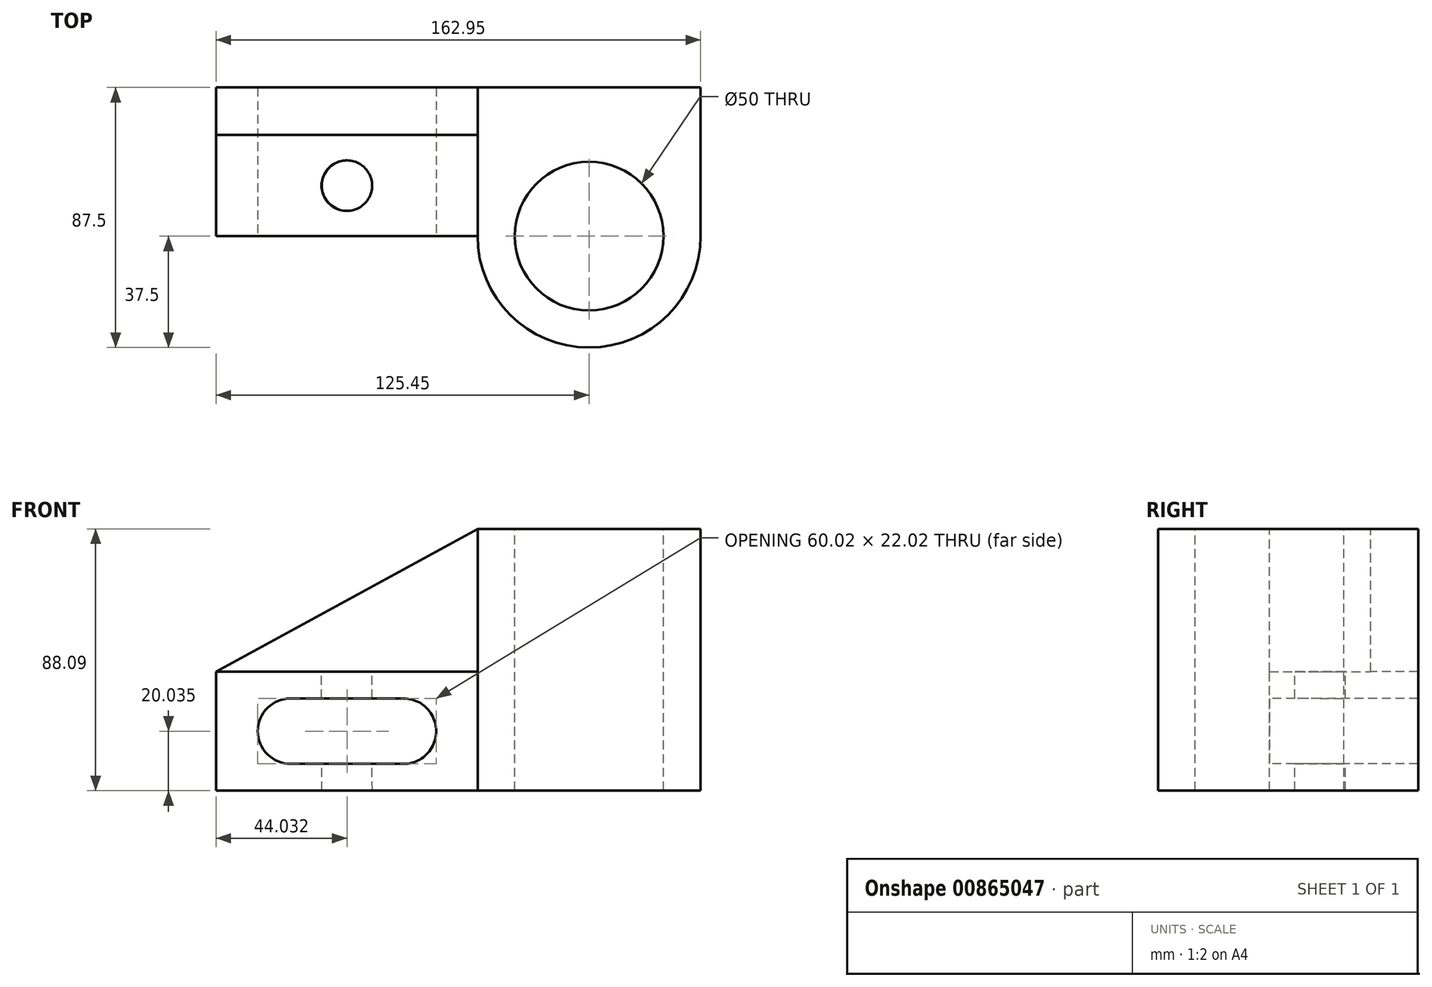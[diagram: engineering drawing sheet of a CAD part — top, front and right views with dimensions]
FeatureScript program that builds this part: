
annotation { "Feature Type Name" : "Feature", "Feature Type Description" : "" }
export const myFeature = defineFeature(function(context is Context, id is Id, definition is map)
    precondition{}
    {
        {
            var Q0;
            Q0=qCreatedBy(makeId("Front.planeOp"),FACE);
            var sketch = newSketch(context, id + "F0", { "sketchPlane" : qUnion([Q0])});
            skLineSegment(sketch, "E0", {"start": v(0, 0) * mm, "end": v(0, 88) * mm});
            skLineSegment(sketch, "E1", {"start": v(-74.9, 0) * mm, "end": v(0, 0) * mm});
            skLineSegment(sketch, "E2", {"start": v(0, 88) * mm, "end": v(-75, 88) * mm});
            skLineSegment(sketch, "E3", {"start": v(-74.9, 0) * mm, "end": v(-75, 88) * mm});
            skSolve(sketch);
        }
        {
            var Q0;
            Q0=makeQuery(id+"F0.imprint","IMPRINT",FACE,{"disambiguationData":[TD([[makeQuery(id+"F0.imprint","IMPRINT",EDGE,{"derivedFrom":sQuery(id+"F0.wireOp",EDGE,"E0")}),1.0]])]});
            extrude(context, id + "F1", {"entities" : qUnion([Q0]), "depth" : 50 * mm, "offsetDistance" : 25 * mm});
        }
        {
            var Q0;
            Q0=makeQuery(id+"F1.opExtrude","SWEPT_FACE",FACE,{"disambiguationData":[OSD([sQuery(id+"F0.wireOp",EDGE,"E2")])]});
            var sketch = newSketch(context, id + "F2", { "sketchPlane" : qUnion([Q0])});
            skArc(sketch, "E4", {"start": v(-75, -50) * mm, "mid": v(-37.5, -87.5) * mm, "end": v(0, -50) * mm});
            skSolve(sketch);
        }
        {
            var Q0;
            Q0=makeQuery(id+"F2.imprint","IMPRINT",FACE,{"disambiguationData":[TD([[makeQuery(id+"F2.imprint","IMPRINT",EDGE,{"derivedFrom":sQuery(id+"F2.wireOp",EDGE,"E4")}),1.0]])]});
            extrude(context, id + "F3", {"entities" : qUnion([Q0]), "operationType" : NewBodyOperationType.ADD, "oppositeDirection" : true, "depth" : 88 * mm, "offsetDistance" : 25 * mm});
        }
        {
            var Q0;
            {var subQ0=sQuery(id+"F0.wireOp",EDGE,"E2");Q0=makeQuery(id+"F3.boolean.opBoolean","MERGE",FACE,{"derivedFrom":[makeQuery(id+"F1.opExtrude","SWEPT_FACE",FACE,{"disambiguationData":[OSD([subQ0])]}),makeQuery(id+"F3.opExtrude","CAP_FACE",FACE,{"disambiguationData":[OSD([subQ0,sQuery(id+"F2.wireOp",EDGE,"E4")])],"isStart":true})]});}
            var sketch = newSketch(context, id + "F4", { "sketchPlane" : qUnion([Q0])});
            skCircle(sketch, "E5", {"center": v(-37.5, -50) * mm, "radius": 25 * mm});
            skSolve(sketch);
        }
        {
            var Q0;
            Q0=makeQuery(id+"F4.imprint","IMPRINT",FACE,{"disambiguationData":[TD([[makeQuery(id+"F4.imprint","IMPRINT",EDGE,{"derivedFrom":sQuery(id+"F4.wireOp",EDGE,"E5")}),1.0]])]});
            extrude(context, id + "F5", {"entities" : qUnion([Q0]), "operationType" : NewBodyOperationType.REMOVE, "oppositeDirection" : true, "depth" : 115 * mm, "offsetDistance" : 25 * mm});
        }
        {
            var Q0;
            Q0=makeQuery(id+"F1.opExtrude","CAP_FACE",FACE,{"disambiguationData":[OSD([sQuery(id+"F0.wireOp",EDGE,"E0"),sQuery(id+"F0.wireOp",EDGE,"E1"),sQuery(id+"F0.wireOp",EDGE,"E2"),sQuery(id+"F0.wireOp",EDGE,"E3")])],"isStart":true});
            var sketch = newSketch(context, id + "F6", { "sketchPlane" : qUnion([Q0])});
            skLineSegment(sketch, "E6", {"start": v(74.9, 0) * mm, "end": v(162.9, -0.1) * mm});
            skLineSegment(sketch, "E7", {"start": v(162.9, -0.1) * mm, "end": v(162.95, 39.9) * mm});
            skLineSegment(sketch, "E8", {"start": v(162.95, 39.9) * mm, "end": v(74.9, 40) * mm});
            skLineSegment(sketch, "E9", {"start": v(74.9, 40) * mm, "end": v(74.9, 0) * mm});
            skSolve(sketch);
        }
        {
            var Q0;
            {var subQ0=sQuery(id+"F6.wireOp",EDGE,"E6");Q0=makeQuery(id+"F6.imprint","IMPRINT",FACE,{"disambiguationData":[TD([[makeQuery(id+"F6.imprint","IMPRINT",EDGE,{"derivedFrom":subQ0}),1.0]])]});}
            extrude(context, id + "F7", {"entities" : qUnion([Q0]), "operationType" : NewBodyOperationType.ADD, "oppositeDirection" : true, "depth" : 50 * mm, "offsetDistance" : 25 * mm});
        }
        {
            var Q0;
            Q0=makeQuery(id+"F1.opExtrude","SWEPT_FACE",FACE,{"disambiguationData":[OSD([sQuery(id+"F0.wireOp",EDGE,"E3")])]});
            var sketch = newSketch(context, id + "F8", { "sketchPlane" : qUnion([Q0])});
            skLineSegment(sketch, "E10", {"start": v(0, 88.08) * mm, "end": v(0, 40.08) * mm});
            skLineSegment(sketch, "E11", {"start": v(0, 40.08) * mm, "end": v(16, 40.08) * mm});
            skLineSegment(sketch, "E12", {"start": v(16, 40.08) * mm, "end": v(16, 88.08) * mm});
            skLineSegment(sketch, "E13", {"start": v(0, 88.08) * mm, "end": v(16, 88.08) * mm});
            skSolve(sketch);
        }
        {
            var Q0;
            Q0=makeQuery(id+"F8.imprint","IMPRINT",FACE,{"disambiguationData":[TD([[makeQuery(id+"F8.imprint","IMPRINT",EDGE,{"derivedFrom":sQuery(id+"F8.wireOp",EDGE,"E10")}),-1.0]])]});
            extrude(context, id + "F9", {"entities" : qUnion([Q0]), "operationType" : NewBodyOperationType.ADD, "depth" : 88 * mm, "offsetDistance" : 25 * mm});
        }
        {
            var Q0;
            Q0=makeQuery(id+"F9.opExtrude","SWEPT_FACE",FACE,{"disambiguationData":[OSD([sQuery(id+"F8.wireOp",EDGE,"E12")])]});
            var sketch = newSketch(context, id + "F10", { "sketchPlane" : qUnion([Q0])});
            skLineSegment(sketch, "E14", {"start": v(-162.95, 39.9) * mm, "end": v(-75, 88) * mm});
            skSolve(sketch);
        }
        {
            var Q0;
            Q0=makeQuery(id+"F10.imprint","IMPRINT",FACE,{"disambiguationData":[TD([[makeQuery(id+"F10.imprint","IMPRINT",EDGE,{"derivedFrom":sQuery(id+"F10.wireOp",EDGE,"E14")}),1.0]])]});
            extrude(context, id + "F11", {"entities" : qUnion([Q0]), "operationType" : NewBodyOperationType.REMOVE, "oppositeDirection" : true, "depth" : 27.7 * mm, "offsetDistance" : 25 * mm});
        }
        {
            var Q0;
            Q0=makeQuery(id+"F7.opExtrude","SWEPT_FACE",FACE,{"disambiguationData":[OSD([sQuery(id+"F6.wireOp",EDGE,"E8")])]});
            var sketch = newSketch(context, id + "F12", { "sketchPlane" : qUnion([Q0])});
            skCircle(sketch, "E15", {"center": v(-118.93, -33) * mm, "radius": 8.5 * mm});
            skPoint(sketch, "E15.centerSnap0", {"position": v(-162.9, -33) * mm});
            skPoint(sketch, "E15.centerSnap1", {"position": v(-118.93, -50) * mm});
            skSolve(sketch);
        }
        {
            var Q0;
            Q0=makeQuery(id+"F12.imprint","IMPRINT",FACE,{"disambiguationData":[TD([[makeQuery(id+"F12.imprint","IMPRINT",EDGE,{"derivedFrom":sQuery(id+"F12.wireOp",EDGE,"E15")}),1.0]])]});
            extrude(context, id + "F13", {"entities" : qUnion([Q0]), "operationType" : NewBodyOperationType.REMOVE, "oppositeDirection" : true, "depth" : 57.3 * mm, "offsetDistance" : 25 * mm});
        }
        {
            var Q0;
            Q0=makeQuery(id+"F7.opExtrude","CAP_FACE",FACE,{"disambiguationData":[OSD([sQuery(id+"F0.wireOp",EDGE,"E3"),sQuery(id+"F6.wireOp",EDGE,"E6"),sQuery(id+"F6.wireOp",EDGE,"E7"),sQuery(id+"F6.wireOp",EDGE,"E8")])],"isStart":false});
            var sketch = newSketch(context, id + "F14", { "sketchPlane" : qUnion([Q0])});
            skLineSegment(sketch, "E16", {"start": v(-118.92, 8.95) * mm, "end": v(-137.92, 8.93) * mm});
            skLineSegment(sketch, "E17", {"start": v(-137.92, 30.95) * mm, "end": v(-118.94, 30.95) * mm});
            skLineSegment(sketch, "E18", {"start": v(-99.93, 30.95) * mm, "end": v(-118.94, 30.95) * mm});
            skLineSegment(sketch, "E19", {"start": v(-99.93, 8.93) * mm, "end": v(-118.92, 8.95) * mm});
            skArc(sketch, "E20", {"start": v(-137.92, 30.95) * mm, "mid": v(-148.93, 19.94) * mm, "end": v(-137.92, 8.93) * mm});
            skArc(sketch, "E21", {"start": v(-99.93, 8.93) * mm, "mid": v(-88.9, 19.94) * mm, "end": v(-99.93, 30.95) * mm});
            skSolve(sketch);
        }
        {
            var Q0;
            Q0=makeQuery(id+"F14.imprint","IMPRINT",FACE,{"disambiguationData":[TD([[makeQuery(id+"F14.imprint","IMPRINT",EDGE,{"derivedFrom":sQuery(id+"F14.wireOp",EDGE,"E16")}),-1.0]])]});
            extrude(context, id + "F15", {"entities" : qUnion([Q0]), "operationType" : NewBodyOperationType.REMOVE, "oppositeDirection" : true, "depth" : 109.8 * mm, "offsetDistance" : 25 * mm});
        }
    });
